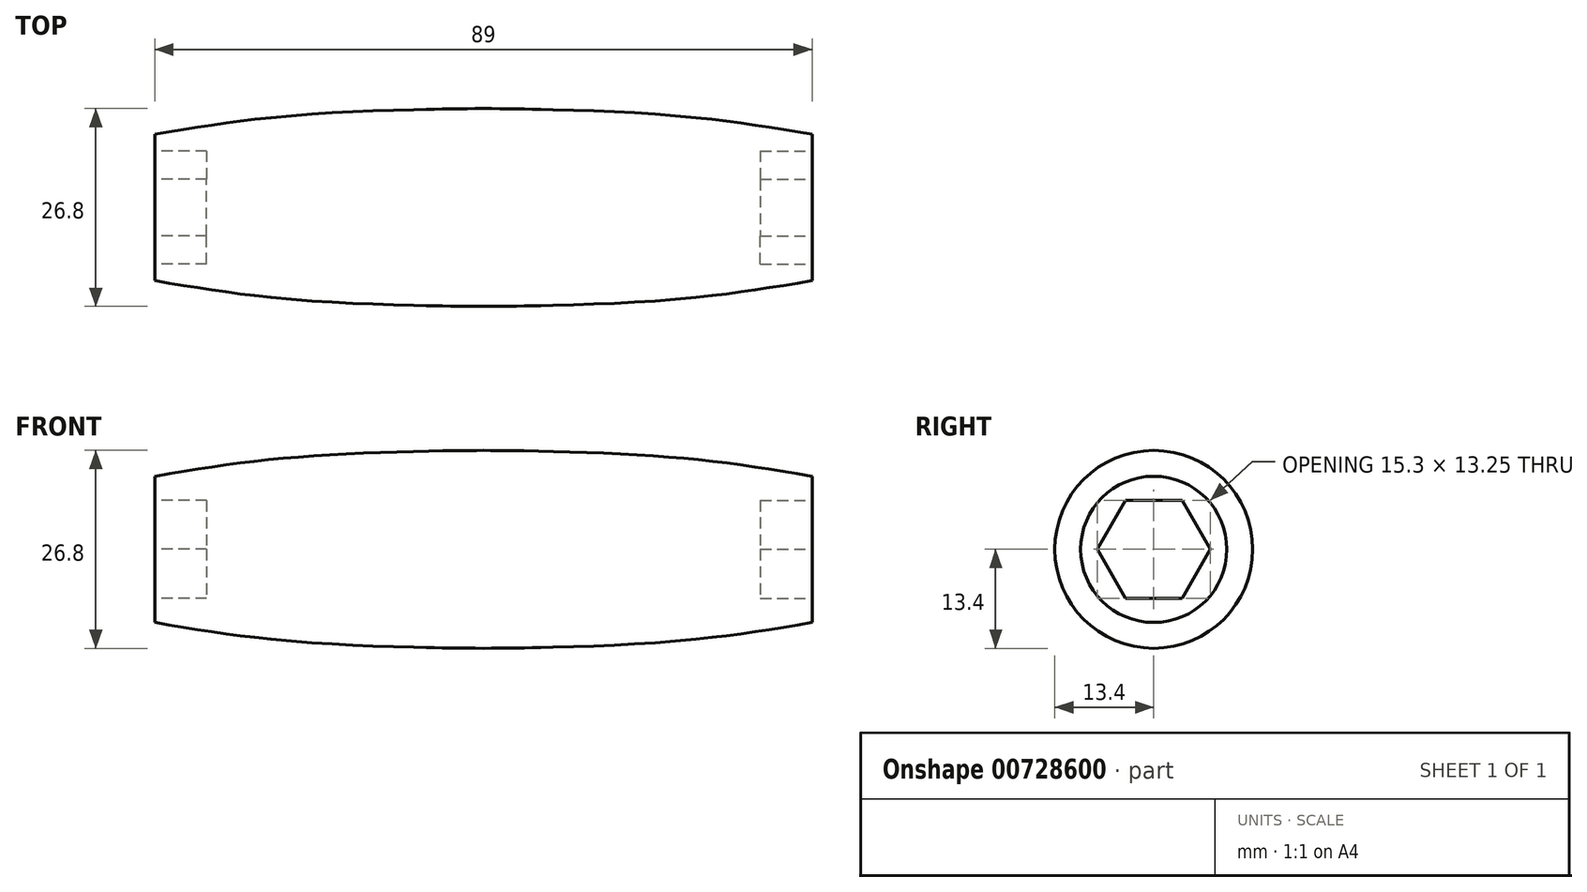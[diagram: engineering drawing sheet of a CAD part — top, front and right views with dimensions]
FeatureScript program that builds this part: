
annotation { "Feature Type Name" : "Feature", "Feature Type Description" : "" }
export const myFeature = defineFeature(function(context is Context, id is Id, definition is map)
    precondition{}
    {
        {
            var Q0;
            Q0=qCreatedBy(makeId("Front.planeOp"),FACE);
            var sketch = newSketch(context, id + "F0", { "sketchPlane" : qUnion([Q0])});
            skLineSegment(sketch, "E0", {"start": v(0, 0) * mm, "end": v(44.5, 0) * mm});
            skLineSegment(sketch, "E1", {"start": v(44.5, 0) * mm, "end": v(44.5, 9.9) * mm});
            skFitSpline(sketch, "E2", {"points": [v(0, 13.4) * mm, v(21.37, 12.77) * mm, v(44.5, 9.9) * mm], "startDerivative": vector(18.35, 0) * mm, "endDerivative": vector(46.67, -8.18) * mm});
            skLineSegment(sketch, "E3", {"start": v(44.5, 0) * mm, "end": v(0, 0) * mm});
            skLineSegment(sketch, "E4", {"start": v(0, 13.4) * mm, "end": v(0, 0) * mm});
            skFitSpline(sketch, "E5.MirrorCS", {"points": [v(0, 13.4) * mm, v(-21.37, 12.77) * mm, v(-44.5, 9.9) * mm], "startDerivative": vector(-18.35, 0) * mm, "endDerivative": vector(-46.67, -8.18) * mm});
            skLineSegment(sketch, "E6.MirrorCS", {"start": v(-44.5, 0) * mm, "end": v(-44.5, 9.9) * mm});
            skLineSegment(sketch, "E7.MirrorCS", {"start": v(-44.5, 0) * mm, "end": v(0, 0) * mm});
            skSolve(sketch);
        }
        {
            var Q0;
            Q0=makeQuery(id+"F0.imprint","IMPRINT",FACE,{"disambiguationData":[TD([[makeQuery(id+"F0.imprint","IMPRINT",EDGE,{"derivedFrom":sQuery(id+"F0.wireOp",EDGE,"E1")}),1.0]])]});
            var Q1;
            Q1=makeQuery(id+"F0.imprint","IMPRINT",FACE,{"disambiguationData":[TD([[makeQuery(id+"F0.imprint","IMPRINT",EDGE,{"derivedFrom":sQuery(id+"F0.wireOp",EDGE,"E4")}),-1.0]])]});
            var Q2;
            Q2=sQuery(id+"F0.wireOp",EDGE,"E0");
            revolve(context, id + "F1", {"surfaceOperationType" : NewSurfaceOperationType.NEW, "entities" : qUnion([Q0, Q1]), "axis" : qUnion([Q2]), "revolveType" : RevolveType.FULL});
        }
        {
            var Q0;
            Q0=makeQuery(id+"F1.opRevolve","SWEPT_FACE",FACE,{"disambiguationData":[OSD([sQuery(id+"F0.wireOp",EDGE,"E1")])]});
            var sketch = newSketch(context, id + "F2", { "sketchPlane" : qUnion([Q0])});
            skCircle(sketch, "E8.cCircle", {"center": v(0, 0) * mm, "radius": 6.62 * mm, "construction": true});
            skLineSegment(sketch, "E8.0", {"start": v(3.82, -6.62) * mm, "end": v(-3.82, -6.62) * mm});
            skLineSegment(sketch, "E8.1", {"start": v(-3.82, -6.63) * mm, "end": v(-7.65, 0) * mm});
            skLineSegment(sketch, "E8.2", {"start": v(-7.65, 0) * mm, "end": v(-3.82, 6.62) * mm});
            skLineSegment(sketch, "E8.3", {"start": v(-3.82, 6.62) * mm, "end": v(3.82, 6.63) * mm});
            skLineSegment(sketch, "E8.4", {"start": v(3.82, 6.63) * mm, "end": v(7.65, 0) * mm});
            skLineSegment(sketch, "E8.5", {"start": v(7.65, 0) * mm, "end": v(3.82, -6.63) * mm});
            skPoint(sketch, "E8.0.midPoint", {"position": v(0, -6.62) * mm});
            skSolve(sketch);
        }
        {
            var Q0;
            Q0 = qSketchRegion(id + "F2", true);
            extrude(context, id + "F3", {"entities" : qUnion([Q0]), "operationType" : NewBodyOperationType.REMOVE, "oppositeDirection" : true, "depth" : 7 * mm, "offsetDistance" : 25 * mm});
        }
        {
            var Q0;
            Q0=makeQuery(id+"F1.opRevolve","SWEPT_FACE",FACE,{"disambiguationData":[OSD([sQuery(id+"F0.wireOp",EDGE,"E6.MirrorCS")])]});
            var sketch = newSketch(context, id + "F4", { "sketchPlane" : qUnion([Q0])});
            skCircle(sketch, "E9.cCircle", {"center": v(0, 0) * mm, "radius": 6.62 * mm, "construction": true});
            skLineSegment(sketch, "E9.0", {"start": v(3.82, -6.62) * mm, "end": v(-3.82, -6.62) * mm});
            skLineSegment(sketch, "E9.1", {"start": v(-3.82, -6.62) * mm, "end": v(-7.65, 0) * mm});
            skLineSegment(sketch, "E9.2", {"start": v(-7.65, 0) * mm, "end": v(-3.82, 6.62) * mm});
            skLineSegment(sketch, "E9.3", {"start": v(-3.82, 6.62) * mm, "end": v(3.82, 6.63) * mm});
            skLineSegment(sketch, "E9.4", {"start": v(3.82, 6.63) * mm, "end": v(7.65, 0) * mm});
            skLineSegment(sketch, "E9.5", {"start": v(7.65, 0) * mm, "end": v(3.82, -6.63) * mm});
            skPoint(sketch, "E9.0.midPoint", {"position": v(0, -6.62) * mm});
            skSolve(sketch);
        }
        {
            var Q0;
            Q0 = qSketchRegion(id + "F4", true);
            extrude(context, id + "F5", {"entities" : qUnion([Q0]), "operationType" : NewBodyOperationType.REMOVE, "oppositeDirection" : true, "depth" : 7 * mm, "offsetDistance" : 25 * mm});
        }
    });
